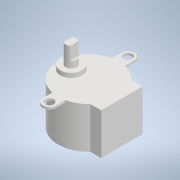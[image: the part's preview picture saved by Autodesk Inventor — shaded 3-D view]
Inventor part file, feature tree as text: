
AUTODESK INVENTOR PART (.ipt)
format: ipt  version: 2022 (Build 260153000, 153)  size: 163,840 bytes
history: native  units: mm
features: extrude x5, sketch x5, projected_geometry x1
ambient origin geometry x8: Origin, YZ Plane, XZ Plane, XY Plane, X Axis, Y Axis, Z Axis, Center Point
bodies: Solid1 (feature_tree)
feature tree (11):
  extrude  "Extrusion1"  Depth=19.0mm TaperAngle=0.0deg
  extrude  "Extrusion2"  Depth=19.0mm
  extrude  "Extrusion3"  Depth=4.0mm
  extrude  "Extrusion4"  Depth=1.0mm TaperAngle=0.0deg
  extrude  "Extrusion5"  Depth=6.0mm
  sketch  "Sketch1"  dims[d0=28.0mm d1=19.0mm d2=0.0mm]
  sketch  "Sketch2"  dims[d3=5.0mm d4=19.0mm]
  sketch  "Sketch3"  dims[d5=4.0mm d6=4.0mm]
  sketch  "Sketch4"  dims[d7=3.0mm d8=1.0mm d9=0.0mm]
  sketch  "Sketch5"  dims[d10=10.0mm d11=6.0mm d12=2.0mm d13=0.0mm d14=5.0mm d15=9.0mm d16=0.0mm d19=3.0mm d20=6.0mm d21=0.0mm]
  projected_geometry  "Projected Loop1"
